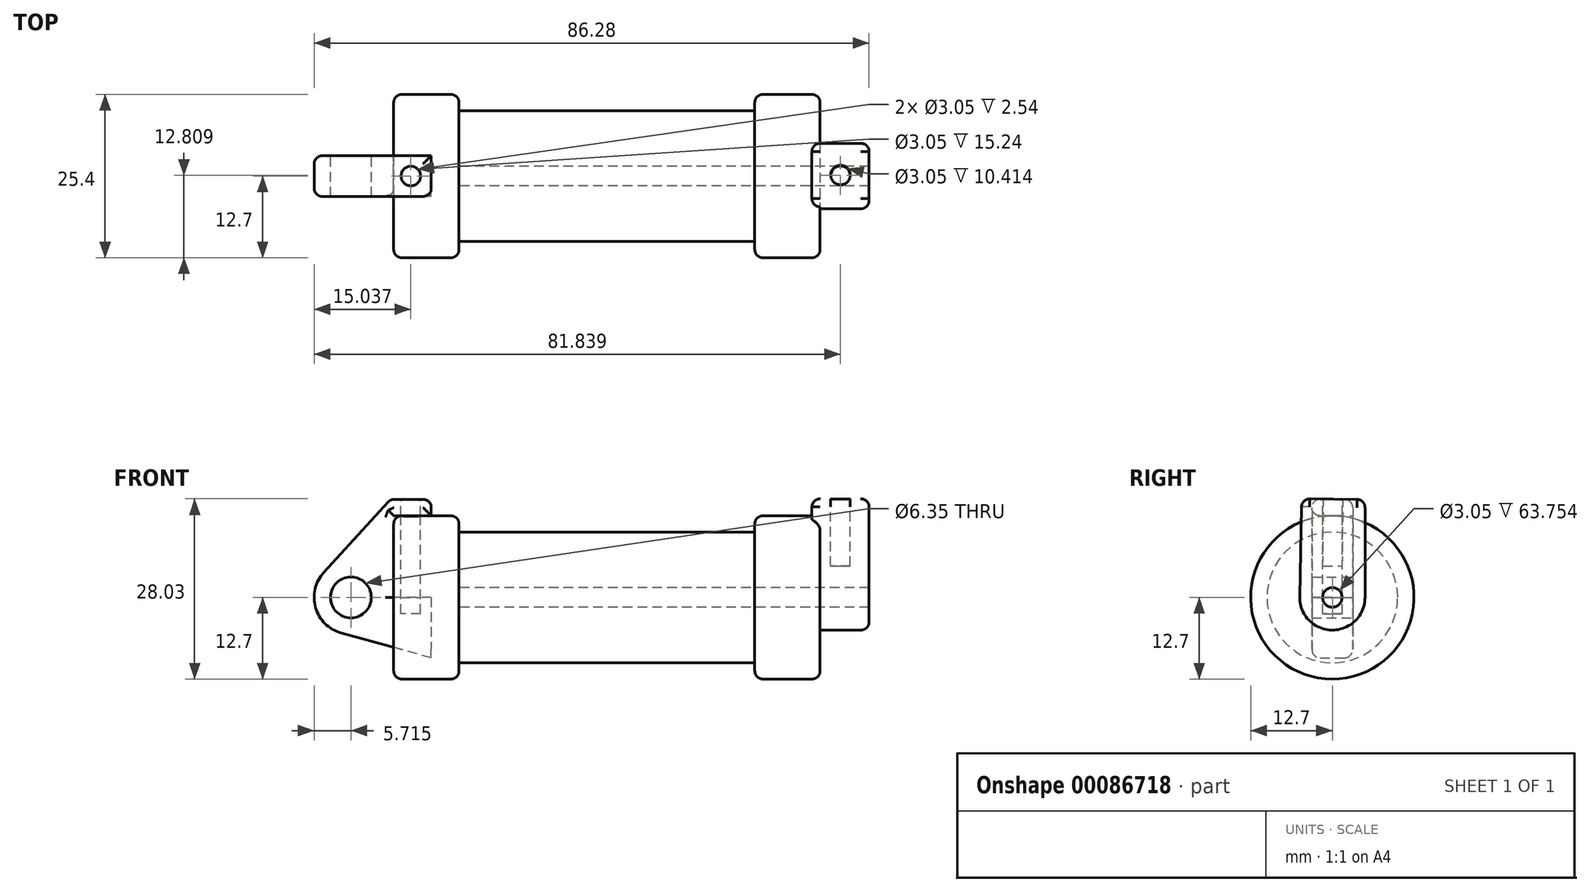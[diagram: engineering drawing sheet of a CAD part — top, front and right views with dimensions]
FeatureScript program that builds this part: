
annotation { "Feature Type Name" : "Feature", "Feature Type Description" : "" }
export const myFeature = defineFeature(function(context is Context, id is Id, definition is map)
    precondition{}
    {
        {
            var Q0;
            Q0=qCreatedBy(makeId("Front.planeOp"),FACE);
            var sketch = newSketch(context, id + "F0", { "sketchPlane" : qUnion([Q0])});
            skLineSegment(sketch, "E0", {"start": v(0, 0) * mm, "end": v(0, 12.7) * mm});
            skLineSegment(sketch, "E1", {"start": v(0, 12.7) * mm, "end": v(10.16, 12.7) * mm});
            skLineSegment(sketch, "E2", {"start": v(10.16, 12.7) * mm, "end": v(10.16, 10.16) * mm});
            skLineSegment(sketch, "E3", {"start": v(10.16, 10.16) * mm, "end": v(56.13, 10.16) * mm});
            skLineSegment(sketch, "E4", {"start": v(56.13, 10.16) * mm, "end": v(56.13, 12.7) * mm});
            skLineSegment(sketch, "E5", {"start": v(56.13, 12.7) * mm, "end": v(66.3, 12.7) * mm});
            skLineSegment(sketch, "E6", {"start": v(66.3, 12.7) * mm, "end": v(66.3, 0) * mm});
            skLineSegment(sketch, "E7", {"start": v(66.3, 0) * mm, "end": v(0, 0) * mm});
            skLineSegment(sketch, "E8", {"start": v(5.84, 15.24) * mm, "end": v(-0.5, 15.24) * mm});
            skLineSegment(sketch, "E9", {"start": v(-0.5, 15.24) * mm, "end": v(-10.88, 3.85) * mm});
            skLineSegment(sketch, "E10", {"start": v(0, 0) * mm, "end": v(-6.65, 0) * mm});
            skCircle(sketch, "E11", {"center": v(-6.65, 0) * mm, "radius": 5.72 * mm});
            skCircle(sketch, "E12", {"center": v(-6.65, 0) * mm, "radius": 3.18 * mm});
            skLineSegment(sketch, "E13", {"start": v(5.84, 15.24) * mm, "end": v(5.84, -9.4) * mm});
            skLineSegment(sketch, "E14", {"start": v(5.84, -9.4) * mm, "end": v(-8.18, -5.5) * mm});
            skSolve(sketch);
        }
        {
            var Q0;
            {var subQ0=sQuery(id+"F0.wireOp",EDGE,"E0");Q0=makeQuery(id+"F0.imprint","IMPRINT",FACE,{"disambiguationData":[TD([[makeQuery(id+"F0.imprint","IMPRINT",EDGE,{"derivedFrom":subQ0}),-1.0]])]});}
            var Q1;
            {var subQ0=sQuery(id+"F0.wireOp",EDGE,"E2");Q1=makeQuery(id+"F0.imprint","IMPRINT",FACE,{"disambiguationData":[TD([[makeQuery(id+"F0.imprint","IMPRINT",EDGE,{"derivedFrom":subQ0}),-1.0]])]});}
            var Q2;
            Q2=sQuery(id+"F0.wireOp",EDGE,"E7");
            revolve(context, id + "F1", {"entities" : qUnion([Q0, Q1]), "axis" : qUnion([Q2]), "revolveType" : RevolveType.FULL});
        }
        {
            var Q0;
            {var subQ4=sQuery(id+"F0.wireOp",EDGE,"E12");Q0=makeQuery(id+"F0.imprint","IMPRINT",FACE,{"disambiguationData":[TD([[makeQuery(id+"F0.imprint","IMPRINT",EDGE,{"derivedFrom":subQ4}),-1.0]])]});}
            var Q1;
            {var subQ3=sQuery(id+"F0.wireOp",EDGE,"E0");Q1=makeQuery(id+"F0.imprint","IMPRINT",FACE,{"disambiguationData":[TD([[makeQuery(id+"F0.imprint","IMPRINT",EDGE,{"derivedFrom":subQ3}),1.0]])]});}
            var Q2;
            {var subQ0=sQuery(id+"F0.wireOp",EDGE,"E14");Q2=makeQuery(id+"F0.imprint","IMPRINT",FACE,{"disambiguationData":[TD([[makeQuery(id+"F0.imprint","IMPRINT",EDGE,{"derivedFrom":subQ0}),-1.0]])]});}
            extrude(context, id + "F2", {"entities" : qUnion([Q0, Q1, Q2]), "endBound" : BoundingType.SYMMETRIC, "depth" : 6.35 * mm});
        }
        {
            var Q0;
            Q0=makeQuery(id+"F1.opRevolve","SWEPT_FACE",FACE,{"disambiguationData":[OSD([sQuery(id+"F0.wireOp",EDGE,"E6")])]});
            var sketch = newSketch(context, id + "F3", { "sketchPlane" : qUnion([Q0])});
            skCircle(sketch, "E15", {"center": v(0, 0) * mm, "radius": 1.52 * mm});
            skCircle(sketch, "E16", {"center": v(0, 0) * mm, "radius": 5.08 * mm});
            skLineSegment(sketch, "E17", {"start": v(5.08, 0) * mm, "end": v(5.08, 15.24) * mm});
            skLineSegment(sketch, "E18", {"start": v(-5.08, 0.1) * mm, "end": v(-4.75, 15.35) * mm});
            skLineSegment(sketch, "E19", {"start": v(-4.75, 15.35) * mm, "end": v(5.08, 15.24) * mm});
            skSolve(sketch);
        }
        {
            var Q0;
            Q0 = qSketchRegion(id + "F3", true);
            extrude(context, id + "F4", {"entities" : qUnion([Q0]), "operationType" : NewBodyOperationType.ADD, "depth" : 7.62 * mm});
        }
        {
            var Q0;
            Q0 = qSketchRegion(id + "F3", true);
            extrude(context, id + "F5", {"entities" : qUnion([Q0]), "operationType" : NewBodyOperationType.ADD, "oppositeDirection" : true, "depth" : 1.27 * mm});
        }
        {
            var Q0;
            Q0=makeQuery(id+"F4.boolean.opBoolean","SPLIT",FACE,{"disambiguationData":[TD([makeQuery(id+"F4.opExtrude","SWEPT_FACE",FACE,{"disambiguationData":[OSD([sQuery(id+"F3.wireOp",EDGE,"E15")])]})])],"derivedFrom":makeQuery(id+"F1.opRevolve","SWEPT_FACE",FACE,{"disambiguationData":[OSD([sQuery(id+"F0.wireOp",EDGE,"E6")])]})});
            var Q1;
            Q1=makeQuery(id+"F1.opRevolve","SWEPT_FACE",FACE,{"disambiguationData":[OSD([sQuery(id+"F0.wireOp",EDGE,"E2")])]});
            extrude(context, id + "F6", {"entities" : qUnion([Q0]), "operationType" : NewBodyOperationType.REMOVE, "endBound" : BoundingType.UP_TO_SURFACE, "oppositeDirection" : true, "endBoundEntityFace" : qUnion([Q1]), "depth" : 50.58 * mm});
        }
        {
            var Q0;
            Q0=makeQuery(id+"F2.opExtrude","SWEPT_FACE",FACE,{"disambiguationData":[OSD([sQuery(id+"F0.wireOp",EDGE,"E8")])]});
            var sketch = newSketch(context, id + "F7", { "sketchPlane" : qUnion([Q0])});
            skCircle(sketch, "E20", {"center": v(2.67, 0) * mm, "radius": 1.52 * mm});
            skPoint(sketch, "E20.centerSnap0", {"position": v(-0.5, 0) * mm});
            skPoint(sketch, "E20.centerSnap1", {"position": v(2.67, 3.18) * mm});
            skSolve(sketch);
        }
        {
            var Q0;
            Q0 = qSketchRegion(id + "F7", true);
            extrude(context, id + "F8", {"entities" : qUnion([Q0]), "operationType" : NewBodyOperationType.REMOVE, "oppositeDirection" : true, "depth" : 17.78 * mm});
        }
        {
            var Q0;
            {var subQ0=sQuery(id+"F3.wireOp",EDGE,"E19");Q0=makeQuery(id+"F5.boolean.opBoolean","MERGE",FACE,{"derivedFrom":[makeQuery(id+"F4.opExtrude","SWEPT_FACE",FACE,{"disambiguationData":[OSD([subQ0])]}),makeQuery(id+"F5.opExtrude","SWEPT_FACE",FACE,{"disambiguationData":[OSD([subQ0])]})]});}
            var sketch = newSketch(context, id + "F9", { "sketchPlane" : qUnion([Q0])});
            skCircle(sketch, "E21", {"center": v(69.47, 0) * mm, "radius": 1.52 * mm});
            skPoint(sketch, "E21.centerSnap0", {"position": v(65.02, 0) * mm});
            skPoint(sketch, "E21.centerSnap1", {"position": v(69.47, 4.92) * mm});
            skSolve(sketch);
        }
        {
            var Q0;
            Q0 = qSketchRegion(id + "F9", true);
            extrude(context, id + "F10", {"entities" : qUnion([Q0]), "operationType" : NewBodyOperationType.REMOVE, "oppositeDirection" : true, "depth" : 10.4 * mm});
        }
        {
            var Q0;
            Q0=makeQuery(id+"F1.opRevolve","SWEPT_EDGE",EDGE,{"disambiguationData":[OSD([sQuery(id+"F0.wireOp",EDGE,"E1"),sQuery(id+"F0.wireOp",EDGE,"E2")])]});
            var Q1;
            Q1=makeQuery(id+"F1.opRevolve","SWEPT_EDGE",EDGE,{"disambiguationData":[OSD([sQuery(id+"F0.wireOp",EDGE,"E0"),sQuery(id+"F0.wireOp",EDGE,"E1")])]});
            var Q2;
            Q2=makeQuery(id+"F1.opRevolve","SWEPT_EDGE",EDGE,{"disambiguationData":[OSD([sQuery(id+"F0.wireOp",EDGE,"E4"),sQuery(id+"F0.wireOp",EDGE,"E5")])]});
            var Q3;
            Q3=makeQuery(id+"F4.boolean.opBoolean","SPLIT",EDGE,{"disambiguationData":[OD(1.0)],"derivedFrom":makeQuery(id+"F1.opRevolve","SWEPT_EDGE",EDGE,{"disambiguationData":[OSD([sQuery(id+"F0.wireOp",EDGE,"E5"),sQuery(id+"F0.wireOp",EDGE,"E6")])]})});
            fillet(context, id + "F11", {"entities" : qUnion([Q0, Q1, Q2, Q3]), "radius" : 1.27 * mm, "tangentPropagation" : true, "allowEdgeOverflow" : false});
        }
        {
            var Q0;
            Q0=makeQuery(id+"F2.opExtrude","CAP_EDGE",EDGE,{"disambiguationData":[OSD([sQuery(id+"F0.wireOp",EDGE,"E8")])],"isStart":false});
            var Q1;
            {var subQ0=sQuery(id+"F0.wireOp",EDGE,"E13");Q1=makeQuery(id+"F2.opExtrude","CAP_EDGE",EDGE,{"disambiguationData":[OSD([subQ0]),TDD([makeQuery(id+"F0.imprint","IMPRINT",EDGE,{"disambiguationData":[TD([[makeQuery(id+"F0.imprint","INTERSECT",VERTEX,{"derivedFrom":[sQuery(id+"F0.wireOp",EDGE,"E8"),subQ0]}),-1.0]])],"derivedFrom":subQ0})])],"isStart":false});}
            var Q2;
            Q2=makeQuery(id+"F2.opExtrude","CAP_EDGE",EDGE,{"disambiguationData":[OSD([sQuery(id+"F0.wireOp",EDGE,"E9")])],"isStart":false});
            var Q3;
            Q3=makeQuery(id+"F2.opExtrude","SWEPT_EDGE",EDGE,{"disambiguationData":[OSD([sQuery(id+"F0.wireOp",EDGE,"E8"),sQuery(id+"F0.wireOp",EDGE,"E13")])]});
            var Q4;
            Q4=makeQuery(id+"F2.opExtrude","CAP_EDGE",EDGE,{"disambiguationData":[OSD([sQuery(id+"F0.wireOp",EDGE,"E8")])],"isStart":true});
            var Q5;
            Q5=makeQuery(id+"F2.opExtrude","SWEPT_EDGE",EDGE,{"disambiguationData":[OSD([sQuery(id+"F0.wireOp",EDGE,"E8"),sQuery(id+"F0.wireOp",EDGE,"E9")])]});
            var Q6;
            Q6=makeQuery(id+"F2.opExtrude","CAP_EDGE",EDGE,{"disambiguationData":[OSD([sQuery(id+"F0.wireOp",EDGE,"E9")])],"isStart":true});
            var Q7;
            Q7=makeQuery(id+"F2.opExtrude","SWEPT_EDGE",EDGE,{"disambiguationData":[OSD([sQuery(id+"F0.wireOp",EDGE,"E9"),sQuery(id+"F0.wireOp",EDGE,"E11")])]});
            var Q8;
            Q8=makeQuery(id+"F2.opExtrude","CAP_EDGE",EDGE,{"disambiguationData":[OSD([sQuery(id+"F0.wireOp",EDGE,"E11")])],"isStart":false});
            var Q9;
            Q9=makeQuery(id+"F2.opExtrude","CAP_EDGE",EDGE,{"disambiguationData":[OSD([sQuery(id+"F0.wireOp",EDGE,"E11")])],"isStart":true});
            var Q10;
            Q10=makeQuery(id+"F2.opExtrude","CAP_EDGE",EDGE,{"disambiguationData":[OSD([sQuery(id+"F0.wireOp",EDGE,"E14")])],"isStart":false});
            var Q11;
            Q11=makeQuery(id+"F2.opExtrude","CAP_EDGE",EDGE,{"disambiguationData":[OSD([sQuery(id+"F0.wireOp",EDGE,"E14")])],"isStart":true});
            var Q12;
            Q12=makeQuery(id+"F2.opExtrude","SWEPT_EDGE",EDGE,{"disambiguationData":[OSD([sQuery(id+"F0.wireOp",EDGE,"E11"),sQuery(id+"F0.wireOp",EDGE,"E14")])]});
            var Q13;
            {var subQ0=sQuery(id+"F0.wireOp",EDGE,"E0");Q13=makeQuery(id+"F11.opFillet","BLEND_EDGE",EDGE,{"blendedFrom":[makeQuery(id+"F1.opRevolve","SWEPT_EDGE",EDGE,{"disambiguationData":[OSD([subQ0,sQuery(id+"F0.wireOp",EDGE,"E1")])]}),makeQuery(id+"F1.opRevolve","SWEPT_FACE",FACE,{"disambiguationData":[OSD([subQ0])]})],"blendedInto":[makeQuery(id+"F1.opRevolve","SWEPT_FACE",FACE,{"disambiguationData":[OSD([subQ0])]})]});}
            var Q14;
            Q14=makeQuery(id+"F2.opExtrude","CAP_EDGE",EDGE,{"disambiguationData":[OSD([sQuery(id+"F0.wireOp",EDGE,"E0")])],"isStart":false});
            var Q15;
            Q15=makeQuery(id+"F2.opExtrude","CAP_EDGE",EDGE,{"disambiguationData":[OSD([sQuery(id+"F0.wireOp",EDGE,"E1")])],"isStart":false});
            fillet(context, id + "F12", {"entities" : qUnion([Q0, Q1, Q2, Q3, Q4, Q5, Q6, Q7, Q8, Q9, Q10, Q11, Q12, Q13, Q14, Q15]), "radius" : 1.27 * mm, "tangentPropagation" : true, "allowEdgeOverflow" : false});
        }
        {
            var Q0;
            Q0=makeQuery(id+"F4.opExtrude","CAP_EDGE",EDGE,{"disambiguationData":[OSD([sQuery(id+"F3.wireOp",EDGE,"E19")])],"isStart":false});
            var Q1;
            {var subQ0=sQuery(id+"F3.wireOp",EDGE,"E19");var subQ1=sQuery(id+"F3.wireOp",EDGE,"E17");Q1=makeQuery(id+"F5.boolean.opBoolean","MERGE",EDGE,{"derivedFrom":[makeQuery(id+"F4.opExtrude","SWEPT_EDGE",EDGE,{"disambiguationData":[OSD([subQ1,subQ0])]}),makeQuery(id+"F5.opExtrude","SWEPT_EDGE",EDGE,{"disambiguationData":[OSD([subQ1,subQ0])]})]});}
            var Q2;
            {var subQ0=sQuery(id+"F3.wireOp",EDGE,"E19");var subQ1=sQuery(id+"F3.wireOp",EDGE,"E18");Q2=makeQuery(id+"F5.boolean.opBoolean","MERGE",EDGE,{"derivedFrom":[makeQuery(id+"F4.opExtrude","SWEPT_EDGE",EDGE,{"disambiguationData":[OSD([subQ1,subQ0])]}),makeQuery(id+"F5.opExtrude","SWEPT_EDGE",EDGE,{"disambiguationData":[OSD([subQ1,subQ0])]})]});}
            var Q3;
            Q3=makeQuery(id+"F5.opExtrude","CAP_EDGE",EDGE,{"disambiguationData":[OSD([sQuery(id+"F3.wireOp",EDGE,"E19")])],"isStart":false});
            fillet(context, id + "F13", {"entities" : qUnion([Q0, Q1, Q2, Q3]), "radius" : 1.27 * mm, "tangentPropagation" : true, "allowEdgeOverflow" : false});
        }
        {
            var Q0;
            Q0=makeQuery(id+"F4.opExtrude","CAP_EDGE",EDGE,{"disambiguationData":[OSD([sQuery(id+"F3.wireOp",EDGE,"E16")])],"isStart":true});
            var Q1;
            Q1=makeQuery(id+"F4.opExtrude","CAP_EDGE",EDGE,{"disambiguationData":[OSD([sQuery(id+"F3.wireOp",EDGE,"E16")])],"isStart":false});
            fillet(context, id + "F14", {"entities" : qUnion([Q0, Q1]), "radius" : 1.27 * mm, "tangentPropagation" : true, "allowEdgeOverflow" : false});
        }
        {
            var Q0;
            Q0=makeQuery(id+"F5.opExtrude","CAP_EDGE",EDGE,{"disambiguationData":[OSD([sQuery(id+"F3.wireOp",EDGE,"E18")])],"isStart":false});
            var Q1;
            Q1=makeQuery(id+"F5.opExtrude","CAP_EDGE",EDGE,{"disambiguationData":[OSD([sQuery(id+"F3.wireOp",EDGE,"E17")])],"isStart":false});
            var Q2;
            {var subQ0=sQuery(id+"F3.wireOp",EDGE,"E18");Q2=makeQuery(id+"F14.opFillet","BLEND_EDGE",EDGE,{"blendedFrom":[makeQuery(id+"F4.opExtrude","CAP_EDGE",EDGE,{"disambiguationData":[OSD([subQ0])],"isStart":false}),makeQuery(id+"F5.boolean.opBoolean","MERGE",FACE,{"derivedFrom":[makeQuery(id+"F4.opExtrude","SWEPT_FACE",FACE,{"disambiguationData":[OSD([subQ0])]}),makeQuery(id+"F5.opExtrude","SWEPT_FACE",FACE,{"disambiguationData":[OSD([subQ0])]})]})],"blendedInto":[makeQuery(id+"F5.boolean.opBoolean","MERGE",FACE,{"derivedFrom":[makeQuery(id+"F4.opExtrude","SWEPT_FACE",FACE,{"disambiguationData":[OSD([subQ0])]}),makeQuery(id+"F5.opExtrude","SWEPT_FACE",FACE,{"disambiguationData":[OSD([subQ0])]})]})]});}
            var Q3;
            {var subQ0=sQuery(id+"F3.wireOp",EDGE,"E17");Q3=makeQuery(id+"F14.opFillet","BLEND_EDGE",EDGE,{"blendedFrom":[makeQuery(id+"F4.opExtrude","CAP_EDGE",EDGE,{"disambiguationData":[OSD([subQ0])],"isStart":false}),makeQuery(id+"F5.boolean.opBoolean","MERGE",FACE,{"derivedFrom":[makeQuery(id+"F4.opExtrude","SWEPT_FACE",FACE,{"disambiguationData":[OSD([subQ0])]}),makeQuery(id+"F5.opExtrude","SWEPT_FACE",FACE,{"disambiguationData":[OSD([subQ0])]})]})],"blendedInto":[makeQuery(id+"F5.boolean.opBoolean","MERGE",FACE,{"derivedFrom":[makeQuery(id+"F4.opExtrude","SWEPT_FACE",FACE,{"disambiguationData":[OSD([subQ0])]}),makeQuery(id+"F5.opExtrude","SWEPT_FACE",FACE,{"disambiguationData":[OSD([subQ0])]})]})]});}
            fillet(context, id + "F15", {"entities" : qUnion([Q0, Q1, Q2, Q3]), "radius" : 1.27 * mm, "tangentPropagation" : true, "allowEdgeOverflow" : false});
        }
    });
